# Revit family: Турникет трипод PERCo_TTR-11А
name_source: partatom
category: Mechanical Equipment
units: mm (PartAtom-declared; Revit-internal decimal feet)

## family parameters
Always vertical = No
Classification = None
Cut with Voids When Loaded = No
Part Type = Normal
Room Calculation Point = No
Round Connector Dimension = Use Diameter
Shared = No
Work Plane-Based = No

## types (1)
- TTR-11A
    Built-in reader = Yes
    Colour = stainless steel
    Current = 6 A
    Dimensions = 800×760×1055 mm
    Electrical connection = 220 B
    Frame = Stainless steel
    Full name = TTR-11А  Motorized Tripod Turnstile with Automatic Anti-Panic Barrier Arms
    Housing_coating = Panel
    IP Code = IP42
    Manufacturer = PERCo
    Material = Turnstile base ─ high-quality stainless steel. Front panel ─ powder-coated metal sheet. The housing upper part ─ laminated plastic with a polycarbonate insert.
    Maximum dimensions of ACS controller = not provided
    Maximum dimensions of installed readers = max. 145×70×28 mm
    Name = TTR-11А Tripod Turnstile
    Number = 1
    Operating temperature = from -40°С to +50°С, under shelter
    Passageway width = 500 mm
    Plank base = Black
    Plank length = 537 mm  [stored 1.76181 ft]
    Plank material = Stainless steel
    Rated power = 150 W
    Throughput rate = 30 persons/min
    Turnstile cover = Black
    URL = https://www.perco.ru
    Unit of measurement = pcs
    Voltage = 24 V
    Weight = max. 75 kg

note: [stored X ft] marks values corroborated as IEEE doubles in the binary element streams (Revit-internal decimal feet)
